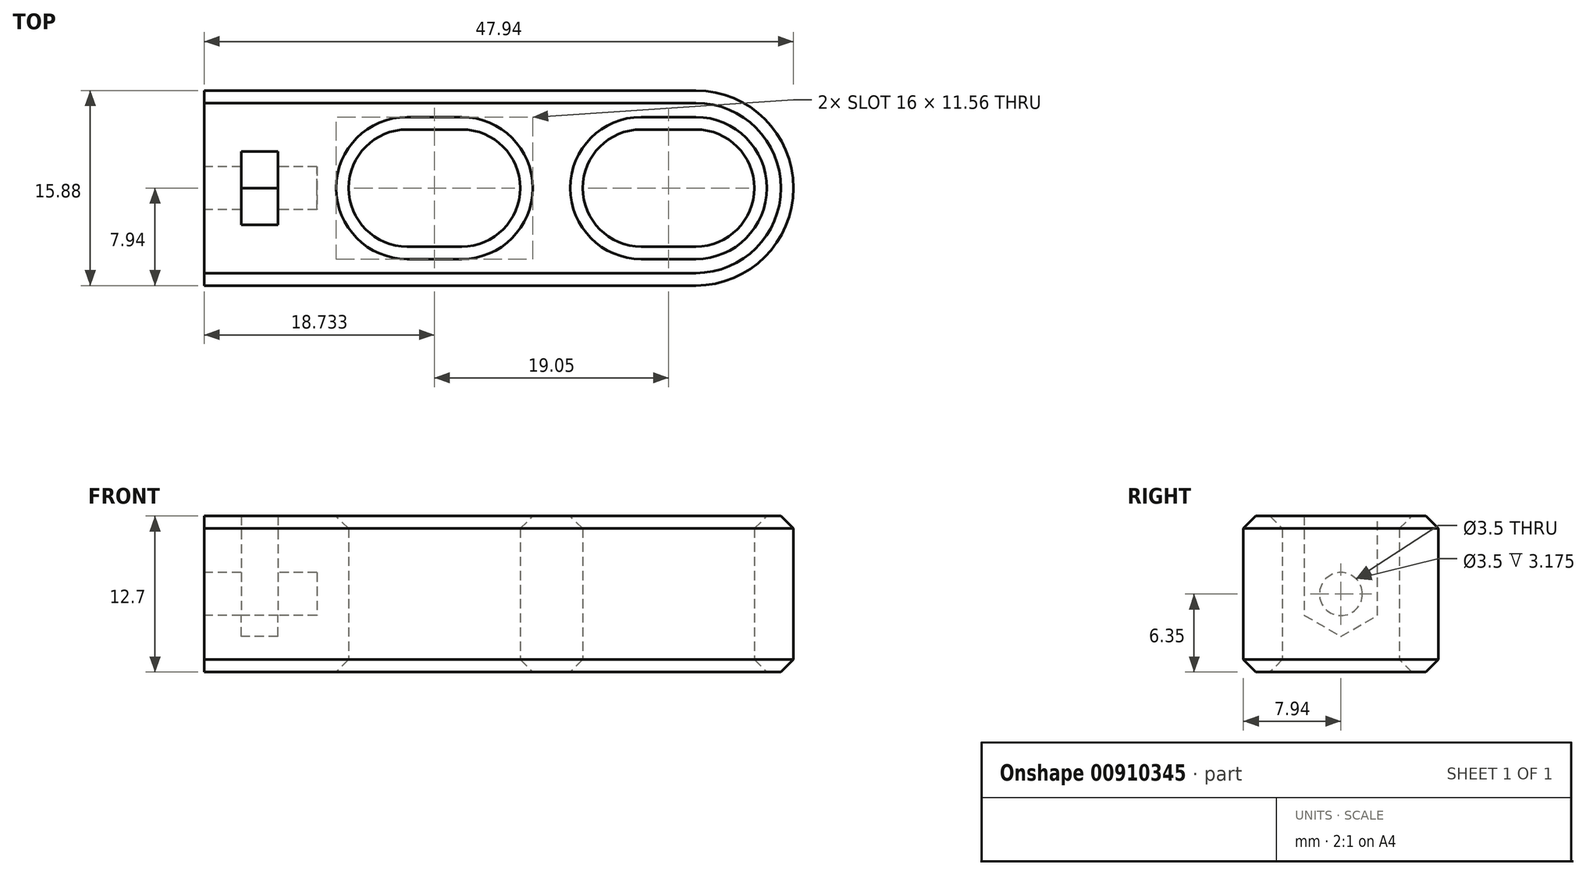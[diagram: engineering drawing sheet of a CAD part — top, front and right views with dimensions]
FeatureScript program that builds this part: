
annotation { "Feature Type Name" : "Feature", "Feature Type Description" : "" }
export const myFeature = defineFeature(function(context is Context, id is Id, definition is map)
    precondition{}
    {
        {
            var Q0;
            Q0=qCreatedBy(makeId("Top.planeOp"),FACE);
            var sketch = newSketch(context, id + "F0", { "sketchPlane" : qUnion([Q0])});
            skLineSegment(sketch, "E0.bottom", {"start": v(0, 7.94) * mm, "end": v(40, 7.94) * mm});
            skLineSegment(sketch, "E0.top", {"start": v(0, -7.94) * mm, "end": v(40, -7.94) * mm});
            skLineSegment(sketch, "E0.left", {"start": v(0, 7.94) * mm, "end": v(0, -7.94) * mm});
            skLineSegment(sketch, "E0.right", {"start": v(40, 7.94) * mm, "end": v(40, -7.94) * mm, "construction": true});
            skArc(sketch, "E1", {"start": v(40, -7.94) * mm, "mid": v(47.94, 0) * mm, "end": v(40, 7.94) * mm});
            skLineSegment(sketch, "E2", {"start": v(16.51, 0) * mm, "end": v(20.96, 0) * mm, "construction": true});
            skLineSegment(sketch, "E3", {"start": v(35.56, 0) * mm, "end": v(40, 0) * mm, "construction": true});
            skArc(sketch, "E4.0.startCap", {"start": v(35.56, -4.76) * mm, "mid": v(30.8, 0) * mm, "end": v(35.56, 4.76) * mm});
            skArc(sketch, "E4.0.endCap", {"start": v(40, 4.76) * mm, "mid": v(44.77, 0) * mm, "end": v(40, -4.76) * mm});
            skLineSegment(sketch, "E4.0.left", {"start": v(35.56, 4.76) * mm, "end": v(40, 4.76) * mm});
            skLineSegment(sketch, "E4.0.right", {"start": v(35.56, -4.76) * mm, "end": v(40, -4.76) * mm});
            skArc(sketch, "E4.1.startCap", {"start": v(16.51, -4.76) * mm, "mid": v(11.75, 0) * mm, "end": v(16.51, 4.76) * mm});
            skArc(sketch, "E4.1.endCap", {"start": v(20.96, 4.76) * mm, "mid": v(25.72, 0) * mm, "end": v(20.96, -4.76) * mm});
            skLineSegment(sketch, "E4.1.left", {"start": v(16.51, 4.76) * mm, "end": v(20.96, 4.76) * mm});
            skLineSegment(sketch, "E4.1.right", {"start": v(16.51, -4.76) * mm, "end": v(20.96, -4.76) * mm});
            skSolve(sketch);
        }
        {
            var Q0;
            Q0 = qSketchRegion(id + "F0", true);
            extrude(context, id + "F1", {"entities" : qUnion([Q0]), "depth" : 12.7 * mm, "offsetDistance" : 25.4 * mm, "symmetric" : true});
        }
        {
            var Q0;
            Q0=makeQuery(id+"F1.opExtrude","SWEPT_FACE",FACE,{"disambiguationData":[OSD([sQuery(id+"F0.wireOp",EDGE,"E0.left")])]});
            var sketch = newSketch(context, id + "F2", { "sketchPlane" : qUnion([Q0])});
            skCircle(sketch, "E5", {"center": v(0, 0) * mm, "radius": 1.75 * mm});
            skSolve(sketch);
        }
        {
            var Q0;
            Q0 = qSketchRegion(id + "F2", true);
            extrude(context, id + "F3", {"entities" : qUnion([Q0]), "operationType" : NewBodyOperationType.REMOVE, "oppositeDirection" : true, "depth" : 3 * mm, "offsetDistance" : 25.4 * mm});
        }
        {
            var Q0;
            Q0=makeQuery(id+"F3.boolean.opBoolean","COPY",FACE,{"derivedFrom":makeQuery(id+"F3.opExtrude","CAP_FACE",FACE,{"disambiguationData":[OSD([sQuery(id+"F2.wireOp",EDGE,"E5")])],"isStart":false})});
            var sketch = newSketch(context, id + "F4", { "sketchPlane" : qUnion([Q0])});
            skCircle(sketch, "E6.cCircle", {"center": v(0, 0) * mm, "radius": 2.98 * mm, "construction": true});
            skLineSegment(sketch, "E6.0", {"start": v(2.98, 1.72) * mm, "end": v(2.98, -1.72) * mm});
            skLineSegment(sketch, "E6.1", {"start": v(2.98, -1.72) * mm, "end": v(0, -3.45) * mm});
            skLineSegment(sketch, "E6.2", {"start": v(0, -3.45) * mm, "end": v(-2.98, -1.72) * mm});
            skLineSegment(sketch, "E6.3", {"start": v(-2.98, -1.72) * mm, "end": v(-2.98, 1.72) * mm});
            skLineSegment(sketch, "E6.4", {"start": v(-2.98, 1.72) * mm, "end": v(0, 3.45) * mm, "construction": true});
            skLineSegment(sketch, "E6.5", {"start": v(0, 3.45) * mm, "end": v(2.98, 1.72) * mm, "construction": true});
            skPoint(sketch, "E6.0.midPoint", {"position": v(2.98, 0) * mm});
            skLineSegment(sketch, "E7", {"start": v(-2.98, 1.72) * mm, "end": v(-2.98, 6.35) * mm});
            skLineSegment(sketch, "E8", {"start": v(-2.98, 6.35) * mm, "end": v(2.98, 6.35) * mm});
            skLineSegment(sketch, "E9", {"start": v(2.98, 6.35) * mm, "end": v(2.98, 1.72) * mm});
            skSolve(sketch);
        }
        {
            var Q0;
            Q0 = qSketchRegion(id + "F4", true);
            extrude(context, id + "F5", {"entities" : qUnion([Q0]), "operationType" : NewBodyOperationType.REMOVE, "oppositeDirection" : true, "depth" : 3 * mm, "offsetDistance" : 25.4 * mm});
        }
        {
            var Q0;
            Q0=makeQuery(id+"F5.boolean.opBoolean","COPY",FACE,{"derivedFrom":makeQuery(id+"F5.opExtrude","CAP_FACE",FACE,{"disambiguationData":[OSD([sQuery(id+"F4.wireOp",EDGE,"E6.0"),sQuery(id+"F4.wireOp",EDGE,"E6.1"),sQuery(id+"F4.wireOp",EDGE,"E6.2"),sQuery(id+"F4.wireOp",EDGE,"E6.3"),sQuery(id+"F4.wireOp",EDGE,"E7"),sQuery(id+"F4.wireOp",EDGE,"E8"),sQuery(id+"F4.wireOp",EDGE,"E9")])],"isStart":false})});
            var sketch = newSketch(context, id + "F6", { "sketchPlane" : qUnion([Q0])});
            skCircle(sketch, "E10.0", {"center": v(0, 0) * mm, "radius": 1.75 * mm});
            skSolve(sketch);
        }
        {
            var Q0;
            Q0 = qSketchRegion(id + "F6", true);
            extrude(context, id + "F7", {"entities" : qUnion([Q0]), "operationType" : NewBodyOperationType.REMOVE, "oppositeDirection" : true, "depth" : 3.17 * mm, "offsetDistance" : 25.4 * mm});
        }
        {
            var Q0;
            Q0=makeQuery(id+"F1.opExtrude","CAP_EDGE",EDGE,{"disambiguationData":[OSD([sQuery(id+"F0.wireOp",EDGE,"E0.top")])],"isStart":false});
            var Q1;
            Q1=makeQuery(id+"F1.opExtrude","CAP_EDGE",EDGE,{"disambiguationData":[OSD([sQuery(id+"F0.wireOp",EDGE,"E0.top")])],"isStart":true});
            var Q2;
            Q2=makeQuery(id+"F1.opExtrude","CAP_EDGE",EDGE,{"disambiguationData":[OSD([sQuery(id+"F0.wireOp",EDGE,"E4.1.endCap")])],"isStart":false});
            var Q3;
            Q3=makeQuery(id+"F1.opExtrude","CAP_EDGE",EDGE,{"disambiguationData":[OSD([sQuery(id+"F0.wireOp",EDGE,"E4.0.startCap")])],"isStart":false});
            var Q4;
            Q4=makeQuery(id+"F1.opExtrude","CAP_EDGE",EDGE,{"disambiguationData":[OSD([sQuery(id+"F0.wireOp",EDGE,"E4.0.startCap")])],"isStart":true});
            var Q5;
            Q5=makeQuery(id+"F1.opExtrude","CAP_EDGE",EDGE,{"disambiguationData":[OSD([sQuery(id+"F0.wireOp",EDGE,"E4.1.endCap")])],"isStart":true});
            chamfer(context, id + "F8", {"entities" : qUnion([Q0, Q1, Q2, Q3, Q4, Q5]), "width" : 1.02 * mm, "tangentPropagation" : true});
        }
    });
